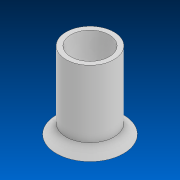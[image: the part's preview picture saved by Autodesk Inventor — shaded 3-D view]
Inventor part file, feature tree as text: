
AUTODESK INVENTOR PART (.ipt)
format: ipt  version: 2022.2 (Build 262287000, 287)  size: 94,720 bytes
history: native  units: in
note: dims shown in document units (in); Inventor stores cm internally (conversion verified against a paired STEP export)
features: revolve x1, sketch x1
ambient origin geometry x8: Origin, YZ Plane, XZ Plane, XY Plane, X Axis, Y Axis, Z Axis, Center Point
bodies: Solid1 (feature_tree)
feature tree (2):
  revolve  "Revolution1"  [1 undecoded]
  sketch  "Sketch2"  dims[d3=2.0in d4=0.5in d5=0.125in d6=45.0deg d7=0.25in d8=90.0deg]
note: 1 required parameter value undecoded (feature->parameter linkage not recoverable at this tier; creation-order binding heuristic only, values carry confidence <= 0.55)
